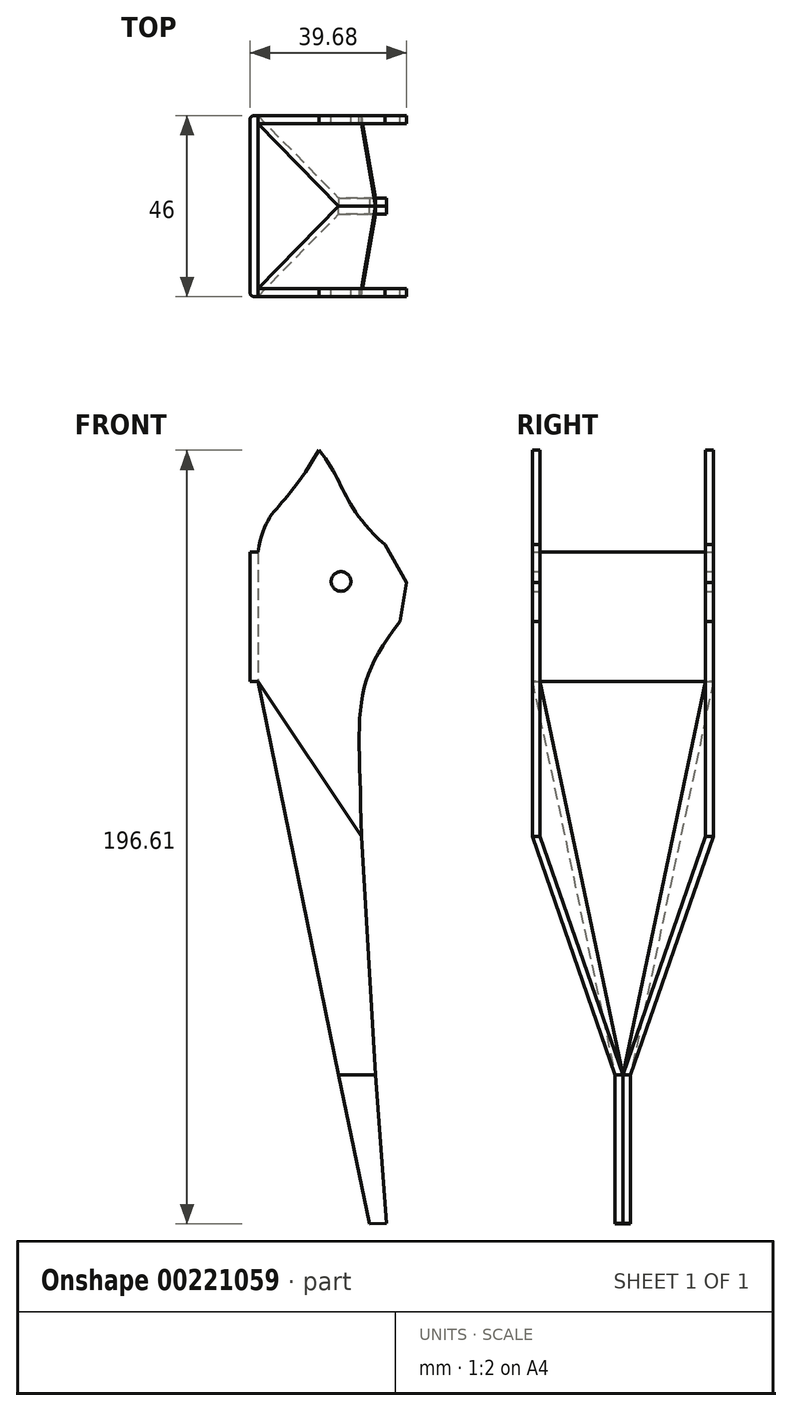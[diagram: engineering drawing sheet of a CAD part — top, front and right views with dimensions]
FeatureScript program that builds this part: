
annotation { "Feature Type Name" : "Feature", "Feature Type Description" : "" }
export const myFeature = defineFeature(function(context is Context, id is Id, definition is map)
    precondition{}
    {
        {
            var Q0;
            Q0=qCreatedBy(makeId("Front.planeOp"),FACE);
            var sketch = newSketch(context, id + "F0", { "sketchPlane" : qUnion([Q0])});
            skLineSegment(sketch, "E0", {"start": v(-57.44, 5.36) * mm, "end": v(-29.1, -132.47) * mm});
            skCircle(sketch, "E1", {"center": v(-36.31, 30.77) * mm, "radius": 2.5 * mm});
            skLineSegment(sketch, "E2", {"start": v(-57.44, 38.23) * mm, "end": v(-57.44, 5.36) * mm});
            skLineSegment(sketch, "E3", {"start": v(-25.18, 40.15) * mm, "end": v(-19.72, 30.45) * mm});
            skLineSegment(sketch, "E4", {"start": v(-57.44, 38.23) * mm, "end": v(-59.4, 38.23) * mm});
            skLineSegment(sketch, "E5", {"start": v(-59.4, 38.23) * mm, "end": v(-59.4, 5.36) * mm});
            skLineSegment(sketch, "E6", {"start": v(-59.4, 5.36) * mm, "end": v(-57.44, 5.36) * mm});
            skLineSegment(sketch, "E7", {"start": v(-19.72, 30.45) * mm, "end": v(-21.3, 20.58) * mm});
            skFitSpline(sketch, "E8", {"points": [v(-21.3, 20.58) * mm, v(-31.14, -35.38) * mm], "startDerivative": vector(-39.68, -51.32) * mm, "endDerivative": vector(1.08, -100.07) * mm});
            skLineSegment(sketch, "E9", {"start": v(-31.7, -35.74) * mm, "end": v(-24.78, -132.25) * mm});
            skLineSegment(sketch, "E10", {"start": v(-29.1, -132.47) * mm, "end": v(-24.78, -132.25) * mm});
            skLineSegment(sketch, "E11", {"start": v(-57.44, 5.36) * mm, "end": v(-31.15, -34.06) * mm});
            skFitSpline(sketch, "E12", {"points": [v(-41.94, 64.14) * mm, v(-25.18, 40.15) * mm], "startDerivative": vector(21.16, -25.4) * mm, "endDerivative": vector(34.39, -30.69) * mm});
            skFitSpline(sketch, "E13", {"points": [v(-41.94, 64.14) * mm, v(-57.44, 38.23) * mm], "startDerivative": vector(-28.04, -49.2) * mm, "endDerivative": vector(-6.11, -36.58) * mm});
            skPoint(sketch, "E14.start.orphan", {"position": v(-38.83, -85.11) * mm});
            skPoint(sketch, "E15.end.orphan", {"position": v(-38.83, -81.77) * mm});
            skLineSegment(sketch, "E16", {"start": v(-27.49, -94.54) * mm, "end": v(-36.9, -94.54) * mm});
            skLineSegment(sketch, "E17", {"start": v(-36.9, -94.54) * mm, "end": v(-37.3, -92.54) * mm});
            skLineSegment(sketch, "E18", {"start": v(-37.3, -92.54) * mm, "end": v(-27.63, -92.54) * mm});
            skSolve(sketch);
        }
        {
            var Q0;
            {var subQ0=sQuery(id+"F0.wireOp",EDGE,"E10");Q0=makeQuery(id+"F0.imprint","IMPRINT",FACE,{"disambiguationData":[TD([[makeQuery(id+"F0.imprint","IMPRINT",EDGE,{"derivedFrom":subQ0}),1.0]])]});}
            extrude(context, id + "F1", {"entities" : qUnion([Q0]), "oppositeDirection" : true, "depth" : 2 * mm});
        }
        {
            var Q0;
            Q0=makeQuery(id+"F0.imprint","IMPRINT",FACE,{"disambiguationData":[TD([[makeQuery(id+"F0.imprint","IMPRINT",EDGE,{"derivedFrom":sQuery(id+"F0.wireOp",EDGE,"E1")}),-1.0]])]});
            var Q1;
            Q1=makeQuery(id+"F0.imprint","IMPRINT",FACE,{"disambiguationData":[TD([[makeQuery(id+"F0.imprint","IMPRINT",EDGE,{"derivedFrom":sQuery(id+"F0.wireOp",EDGE,"E2")}),-1.0]])]});
            extrude(context, id + "F2", {"entities" : qUnion([Q0, Q1]), "endBound" : BoundingType.SYMMETRIC, "depth" : 46 * mm});
        }
        {
            var Q0;
            Q0=makeQuery(id+"F0.imprint","IMPRINT",FACE,{"disambiguationData":[TD([[makeQuery(id+"F0.imprint","IMPRINT",EDGE,{"derivedFrom":sQuery(id+"F0.wireOp",EDGE,"E1")}),-1.0]])]});
            extrude(context, id + "F3", {"entities" : qUnion([Q0]), "operationType" : NewBodyOperationType.REMOVE, "endBound" : BoundingType.SYMMETRIC, "depth" : 42 * mm});
        }
        {
            var Q0;
            {var subQ0=sQuery(id+"F0.wireOp",EDGE,"E13");var subQ1=sQuery(id+"F0.wireOp",EDGE,"E12");var subQ2=sQuery(id+"F0.wireOp",EDGE,"E11");var subQ3=sQuery(id+"F0.wireOp",EDGE,"E8");var subQ4=sQuery(id+"F0.wireOp",EDGE,"E7");var subQ5=sQuery(id+"F0.wireOp",EDGE,"E3");var subQ6=sQuery(id+"F0.wireOp",EDGE,"E2");var subQ7=sQuery(id+"F0.wireOp",EDGE,"E1");Q0=makeQuery(id+"F3.boolean.opBoolean","SPLIT",FACE,{"disambiguationData":[TD([makeQuery(id+"F3.opExtrude","CAP_FACE",FACE,{"disambiguationData":[OSD([subQ7,subQ6,subQ5,subQ4,subQ3,subQ2,subQ1,subQ0])],"isStart":true})])],"derivedFrom":makeQuery(id+"F2.opExtrude","SWEPT_FACE",FACE,{"disambiguationData":[OSD([subQ2])]})});}
            var Q1;
            {var subQ0=sQuery(id+"F0.wireOp",EDGE,"E9");var subQ1=sQuery(id+"F0.wireOp",EDGE,"E16");var subQ2=sQuery(id+"F0.wireOp",EDGE,"E0");Q1=makeQuery(id+"FlpuHt3dEil0ecl_2.boolean.opBoolean","SPLIT",FACE,{"disambiguationData":[TD([makeQuery(id+"F1.opExtrude","CAP_FACE",FACE,{"disambiguationData":[OSD([subQ2,subQ0,sQuery(id+"F0.wireOp",EDGE,"E10"),subQ1])],"isStart":true})])],"derivedFrom":makeQuery(id+"F1.opExtrude","SWEPT_FACE",FACE,{"disambiguationData":[OSD([subQ1])]})});}
            loft(context, id + "F4", {"sheetProfilesArray" : [{ "sheetProfileEntities" : qUnion([Q0]) }, { "sheetProfileEntities" : qUnion([Q1]) }]});
        }
        {
            var Q0;
            {var subQ0=sQuery(id+"F0.wireOp",EDGE,"E10");Q0=makeQuery(id+"F0.imprint","IMPRINT",FACE,{"disambiguationData":[TD([[makeQuery(id+"F0.imprint","IMPRINT",EDGE,{"derivedFrom":subQ0}),1.0]])]});}
            extrude(context, id + "F5", {"entities" : qUnion([Q0]), "depth" : 2 * mm});
        }
        {
            var Q0;
            {var subQ0=sQuery(id+"F0.wireOp",EDGE,"E8");var subQ1=sQuery(id+"F0.wireOp",EDGE,"E13");var subQ2=sQuery(id+"F0.wireOp",EDGE,"E12");var subQ3=sQuery(id+"F0.wireOp",EDGE,"E11");var subQ4=sQuery(id+"F0.wireOp",EDGE,"E7");var subQ5=sQuery(id+"F0.wireOp",EDGE,"E3");var subQ6=sQuery(id+"F0.wireOp",EDGE,"E2");var subQ7=sQuery(id+"F0.wireOp",EDGE,"E1");Q0=makeQuery(id+"F3.boolean.opBoolean","SPLIT",FACE,{"disambiguationData":[TD([makeQuery(id+"F3.opExtrude","CAP_FACE",FACE,{"disambiguationData":[OSD([subQ7,subQ6,subQ5,subQ4,subQ0,subQ3,subQ2,subQ1])],"isStart":false})])],"derivedFrom":makeQuery(id+"F2.opExtrude","SWEPT_FACE",FACE,{"disambiguationData":[OSD([subQ3])]})});}
            var Q1;
            Q1=makeQuery(id+"F5.opExtrude","SWEPT_FACE",FACE,{"disambiguationData":[OSD([sQuery(id+"F0.wireOp",EDGE,"E16")])]});
            loft(context, id + "F6", {"sheetProfilesArray" : [{ "sheetProfileEntities" : qUnion([Q0]) }, { "sheetProfileEntities" : qUnion([Q1]) }]});
        }
        {
            var Q0;
            Q0=makeQuery(id+"F2.opExtrude","CAP_EDGE",EDGE,{"disambiguationData":[OSD([sQuery(id+"F0.wireOp",EDGE,"E5")])],"isStart":false});
            var Q1;
            Q1=makeQuery(id+"F2.opExtrude","CAP_EDGE",EDGE,{"disambiguationData":[OSD([sQuery(id+"F0.wireOp",EDGE,"E5")])],"isStart":true});
            fillet(context, id + "F7", {"entities" : qUnion([Q0, Q1]), "radius" : 1 * mm, "tangentPropagation" : true, "allowEdgeOverflow" : false});
        }
    });
